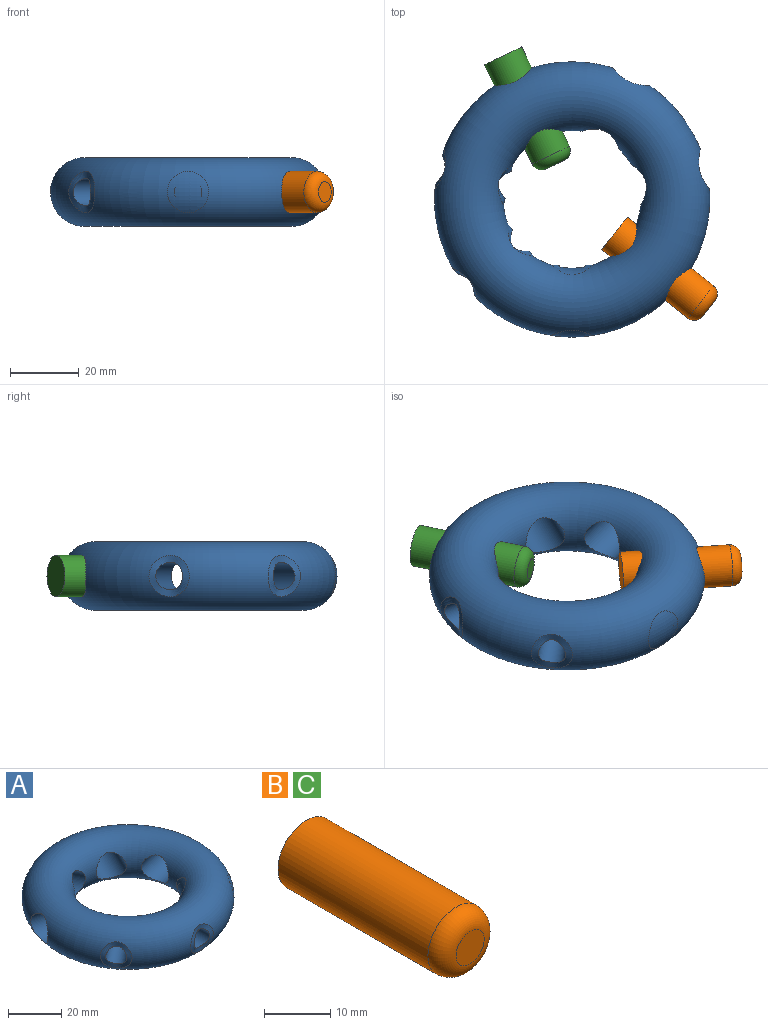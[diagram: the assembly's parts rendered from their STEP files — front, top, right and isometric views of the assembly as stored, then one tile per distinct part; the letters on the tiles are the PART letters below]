
ASSEMBLY  parts=3 mates=2
PART A: 16 faces, bbox 86.6x86.6x20 mm
  f0: torus R=30mm, axis (0,0,1), area 10396.2mm2, adj f1,f3,f4,f5,f6,f7,f8,f10
  f1: bspline ~11.99x11.99mm, area 68mm2, adj f0,f2
  f2: cylinder r=4mm len=20.47mm, axis (0,-1,0), area 459.3mm2, adj f1,f3
  f3: bspline ~11.99x11.99mm, area 64.3mm2, adj f0,f2
  f4: cylinder r=6mm len=22.63mm, axis (0.97,0.22,0), area 688.8mm2, adj f0
  f5: cylinder r=6mm len=23.65mm, axis (0.43,0.9,0), area 689mm2, adj f0
  f6: cylinder r=6mm len=23.65mm, axis (-0.43,0.9,0), area 688.9mm2, adj f0
  f7: cylinder r=6mm len=22.52mm, axis (-0.97,0.22,0), area 713mm2, adj f0
  f8: bspline ~11.99x9.38mm, area 68mm2, adj f0,f9
  f9: cylinder r=4mm len=20.99mm, axis (-0.78,-0.62,0), area 459.3mm2, adj f8,f10
  f10: bspline ~11.99x9.37mm, area 64.3mm2, adj f0,f9
  f11: torus R=30mm, axis (0,0,1), area 121.2mm2, adj f12
  f12: bspline ~11.99x9.38mm, area 68mm2, adj f11,f13
  f13: cylinder r=4mm len=20.99mm, axis (0.78,-0.62,0), area 459.3mm2, adj f12,f14
  f14: bspline ~11.99x9.38mm, area 64.3mm2, adj f13,f15
  f15: torus R=30mm, axis (0,0,1), area 119.3mm2, adj f14
PART B: 4 faces, bbox 13x35x13 mm
  f0: cylinder r=6mm len=32mm, axis (0,1,0), area 1206.4mm2, adj f2,f3
  f1: plane 6x6mm, normal (0,-1,0), area 28.3mm2, adj f3
  f2: plane 12x12mm, normal (0,1,0), area 113.1mm2, adj f0
  f3: torus R=3mm, axis (0,-1,0), area 145.4mm2, adj f0,f1
PART C: same geometry as B
PLACE A rot(axis=(0,0,-1),51.4deg) t=(31.95,20.3,0.62)mm fixed
PLACE B rot(axis=(-0.4,0.83,0.4),100.9deg) t=(44.3,10.46,77.16)mm
PLACE C rot(axis=(0,0,1),25.7deg) t=(-57.08,28.79,0.62)mm
MATE slider A.f4 <-> B.f0  axis (0.78,-0.62,0) through (46.75,8.5,0.62)mm
MATE slider A.f7 <-> C.f0  axis (-0.43,0.9,0) through (23.73,37.36,0.62)mm
